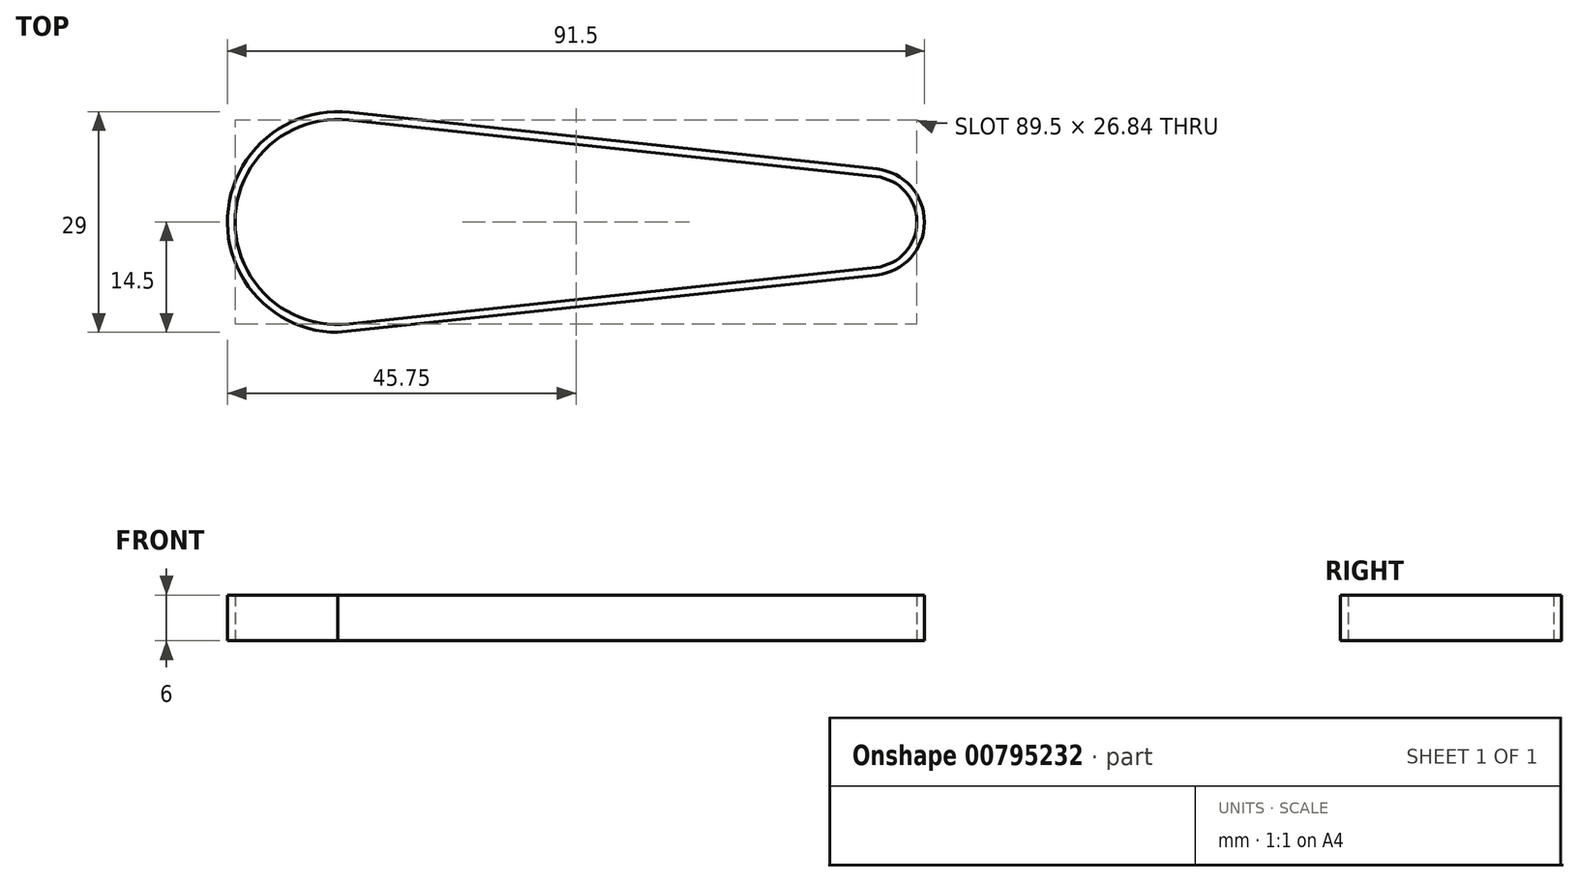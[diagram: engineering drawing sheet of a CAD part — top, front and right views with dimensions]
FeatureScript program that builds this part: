
annotation { "Feature Type Name" : "Feature", "Feature Type Description" : "" }
export const myFeature = defineFeature(function(context is Context, id is Id, definition is map)
    precondition{}
    {
        {
            var Q0;
            Q0=qCreatedBy(makeId("Top.planeOp"),FACE);
            var sketch = newSketch(context, id + "F0", { "sketchPlane" : qUnion([Q0])});
            skArc(sketch, "E0", {"start": v(1.45, 13.42) * mm, "mid": v(-13.5, 0) * mm, "end": v(1.45, -13.42) * mm});
            skArc(sketch, "E1", {"start": v(70.64, -5.97) * mm, "mid": v(76, 0) * mm, "end": v(70.64, 5.97) * mm});
            skLineSegment(sketch, "E2", {"start": v(1.45, 13.42) * mm, "end": v(70.64, 5.97) * mm});
            skLineSegment(sketch, "E3.0", {"start": v(1.55, 14.42) * mm, "end": v(70.75, 6.96) * mm});
            skArc(sketch, "E3.1", {"start": v(1.55, 14.42) * mm, "mid": v(-14.48, 0.78) * mm, "end": v(0, -14.5) * mm});
            skArc(sketch, "E4.trimOffspring", {"start": v(70.74, -6.96) * mm, "mid": v(77, 0) * mm, "end": v(70.75, 6.96) * mm});
            skLineSegment(sketch, "E5", {"start": v(0, -14.5) * mm, "end": v(70.74, -6.96) * mm});
            skLineSegment(sketch, "E6", {"start": v(70.64, -5.97) * mm, "end": v(1.45, -13.42) * mm});
            skSolve(sketch);
        }
        {
            var Q0;
            Q0 = qSketchRegion(id + "F0", true);
            extrude(context, id + "F1", {"entities" : qUnion([Q0]), "depth" : 6 * mm, "offsetDistance" : 25 * mm});
        }
    });
